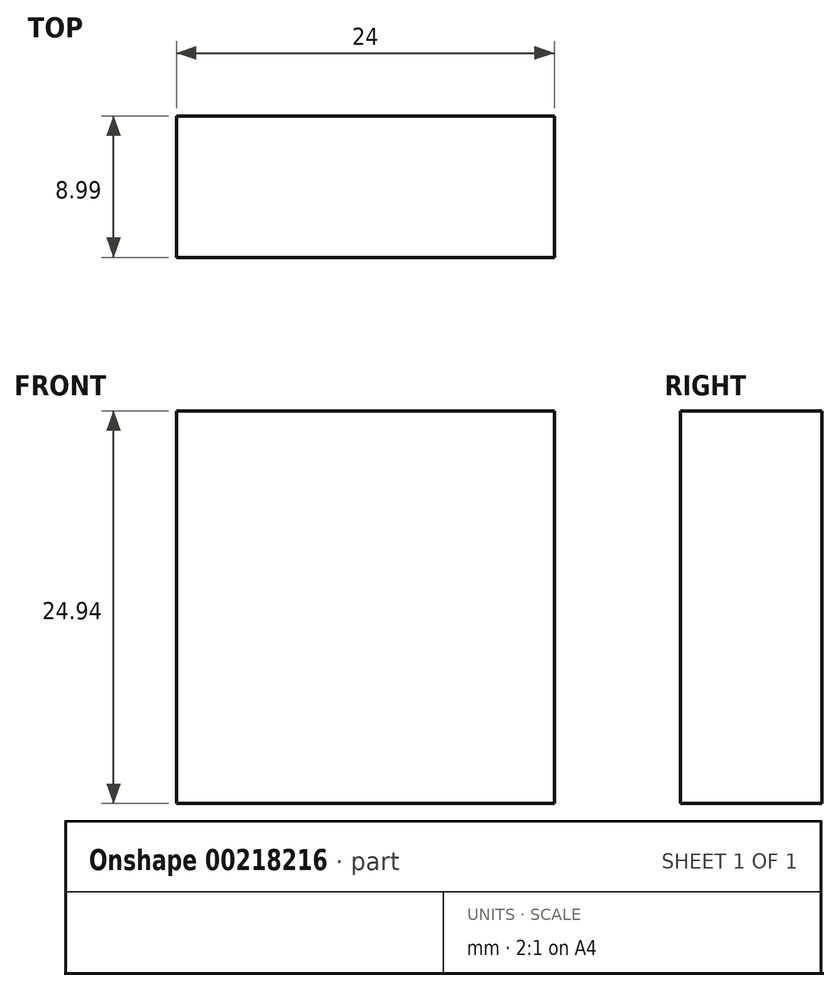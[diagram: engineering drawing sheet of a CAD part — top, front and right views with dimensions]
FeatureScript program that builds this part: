
annotation { "Feature Type Name" : "Feature", "Feature Type Description" : "" }
export const myFeature = defineFeature(function(context is Context, id is Id, definition is map)
    precondition{}
    {
        {
            var Q0;
            Q0=qCreatedBy(makeId("Top.planeOp"),FACE);
            var sketch = newSketch(context, id + "F0", { "sketchPlane" : qUnion([Q0])});
            skLineSegment(sketch, "E0.bottom", {"start": v(0, 0) * mm, "end": v(56, 0) * mm});
            skLineSegment(sketch, "E0.top", {"start": v(0, 37) * mm, "end": v(16, 37) * mm});
            skLineSegment(sketch, "E0.left", {"start": v(0, 0) * mm, "end": v(0, 37) * mm});
            skLineSegment(sketch, "E0.right", {"start": v(56, 0) * mm, "end": v(56, 37) * mm});
            skLineSegment(sketch, "E1.bottom", {"start": v(0, 0) * mm, "end": v(24, 0) * mm});
            skLineSegment(sketch, "E1.top", {"start": v(0, 9) * mm, "end": v(24, 9) * mm});
            skLineSegment(sketch, "E1.left", {"start": v(0, 0) * mm, "end": v(0, 9) * mm});
            skLineSegment(sketch, "E1.right", {"start": v(24, 0) * mm, "end": v(24, 9) * mm});
            skLineSegment(sketch, "E2.left", {"start": v(0, 37) * mm, "end": v(0, 25.02) * mm});
            skLineSegment(sketch, "E2.right", {"start": v(16, 37) * mm, "end": v(16, 25.02) * mm});
            skLineSegment(sketch, "E3.bottom", {"start": v(56, 37) * mm, "end": v(40, 37) * mm});
            skLineSegment(sketch, "E3.left", {"start": v(56, 37) * mm, "end": v(56, 25.02) * mm});
            skLineSegment(sketch, "E3.right", {"start": v(40, 37) * mm, "end": v(40, 25.02) * mm});
            skLineSegment(sketch, "E4", {"start": v(16, 25.02) * mm, "end": v(40, 25.02) * mm});
            skLineSegment(sketch, "E5.trimOffspring", {"start": v(40, 37) * mm, "end": v(56, 37) * mm});
            skSolve(sketch);
        }
        {
            var Q0;
            Q0=makeQuery(id+"F0.imprint","IMPRINT",FACE,{"disambiguationData":[TD([[makeQuery(id+"F0.imprint","IMPRINT",EDGE,{"derivedFrom":sQuery(id+"F0.wireOp",EDGE,"E0.bottom")}),1.0]])]});
            extrude(context, id + "F1", {"entities" : qUnion([Q0]), "depth" : 24.94 * mm});
        }
    });
